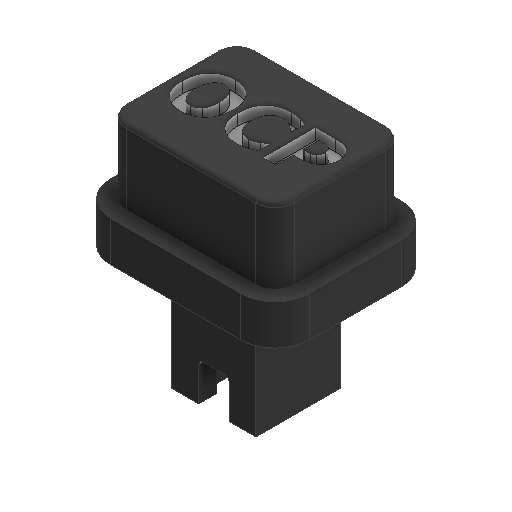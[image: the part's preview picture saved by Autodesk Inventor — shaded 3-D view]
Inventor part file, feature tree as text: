
AUTODESK INVENTOR PART (.ipt)
format: ipt  version: 2025 (Build 290162000, 162)  size: 373,760 bytes
history: native  units: mm
features: sketch x7, extrude x6, fillet x5, mirror x1, emboss x1, plane x1
ambient origin geometry x8: Origin, YZ Plane, XZ Plane, XY Plane, X Axis, Y Axis, Z Axis, Center Point
bodies: Solid1 (feature_tree)
feature tree (21):
  extrude  "Extrusion1"  Depth=6.0mm TaperAngle=0.0deg
  extrude  "Extrusion2"  Depth=2.8mm TaperAngle=0.0deg
  extrude  "Extrusion3"  Depth=2.0mm
  extrude  "Extrusion4"  Depth=0.1mm
  mirror  "Mirror1"
  extrude  "Extrusion5"  Depth=0.14mm
  fillet  "Fillet1"  [1 undecoded]
  fillet  "Fillet2"  Radius=6.8mm
  extrude  "Extrusion6"  Depth=6.0mm TaperAngle=0.0deg
  fillet  "Fillet3"  Radius=1.0mm
  fillet  "Fillet4"  Radius=0.2mm
  fillet  "Fillet5"  Radius=0.8mm
  emboss  "Emboss1"
  sketch  "Sketch1"  dims[d0=4.4mm d1=6.0mm d2=0.0mm]
  sketch  "Sketch2"  dims[d3=2.5mm d4=2.8mm d5=0.0mm]
  sketch  "Sketch3"  dims[d6=1.6mm d7=2.0mm]
  sketch  "Sketch4"  dims[d8=0.0mm d9=0.0mm d13=0.1mm]
  plane  "Work Plane1"
  sketch  "Sketch5"  dims[d14=1.9mm d15=0.14mm d16=0.0mm d17=0.0mm d18=6.8mm]
  sketch  "Sketch6"  dims[d19=8.8mm d20=6.0mm d21=0.0mm d22=1.0mm d23=0.2mm d24=0.8mm]
  sketch  "Sketch7"  dims[d25=2.1mm d26=0.0mm d27=0.6mm d28=30.0deg d29=0.105946mm d30=1.9mm d31=0.2mm d32=0.2mm d33=0.4mm d34=0.5mm d35=0.6mm d36=0.0mm d37=1.95mm]
note: 1 required parameter value undecoded (feature->parameter linkage not recoverable at this tier; creation-order binding heuristic only, values carry confidence <= 0.55)
